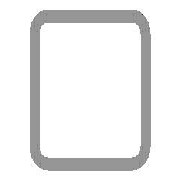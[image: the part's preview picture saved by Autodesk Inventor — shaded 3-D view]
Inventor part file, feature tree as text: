
AUTODESK INVENTOR PART (.ipt)
format: ipt  version: 2025 (Build 290162010, 162A)  size: 135,168 bytes
history: native  units: mm (DEFAULTED — no unit token found)
features: other x4, sketch x1, plane x1
ambient origin geometry x8: Origin, YZ Plane, XZ Plane, XY Plane, X Axis, Y Axis, Z Axis, Center Point
bodies: Solid1 (feature_tree), Body (feature_tree)
feature tree (6):
  parser-record x1  (decoder bookkeeping rows leaked as tree rows — omitted from the tree; the rows remain in map.json)
  other  "Driven Length"
  other  "Start Plane"
  other  "End Plane"
  sketch  "Sketch3"  dims[d3=898.0mm d4=0.0mm d7=4.0mm d9=40.0mm d11=40.0mm d12=2.0mm d13=-0.0mm d14=898.0mm d15=20.0mm d16=20.0mm d17=90.0deg d18=898.0mm]
  plane  "Work Plane3"
